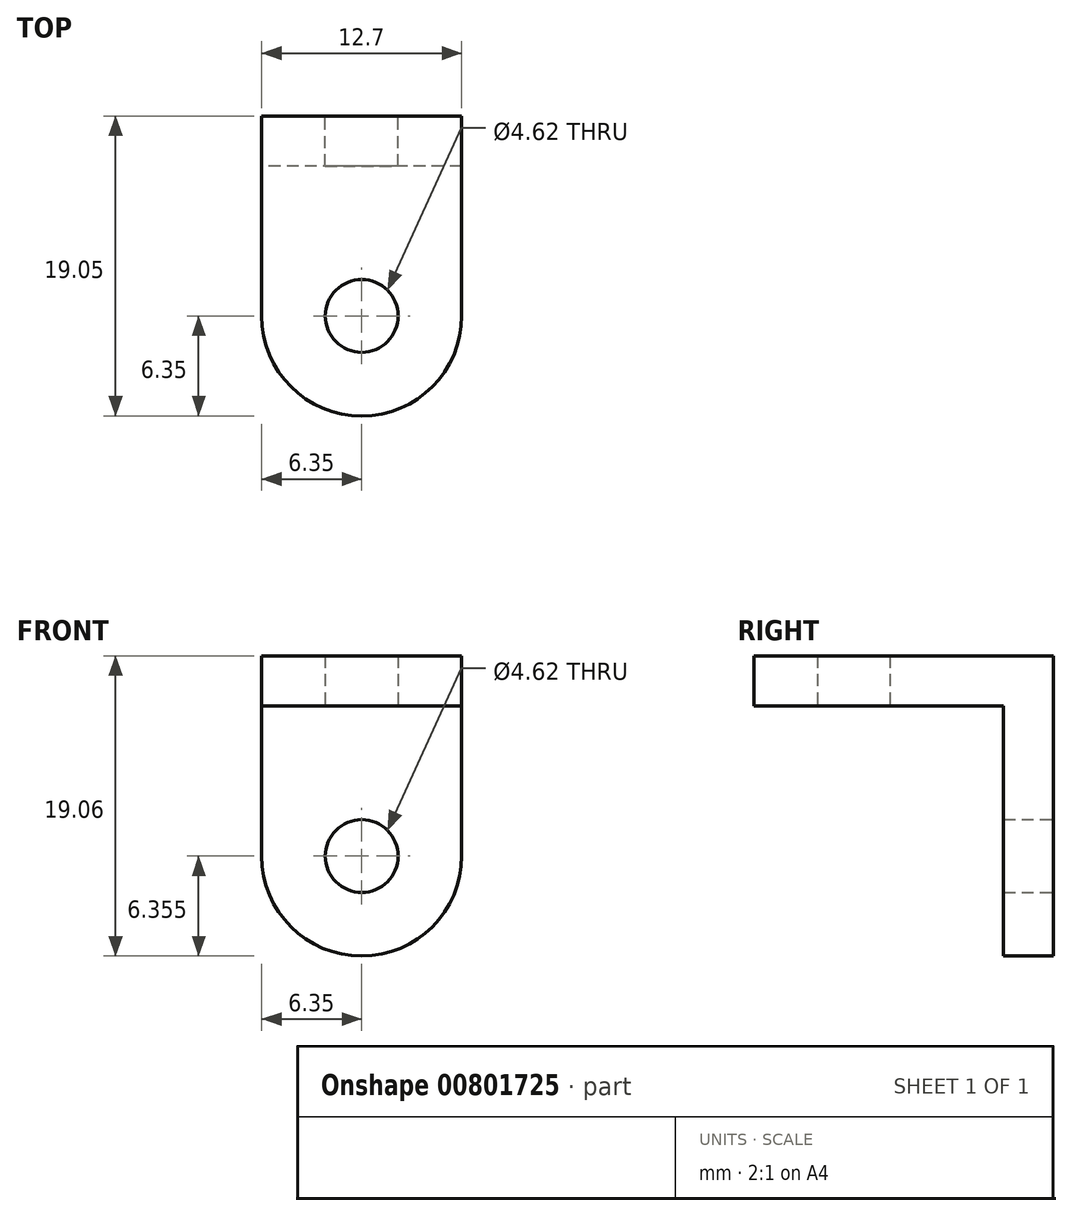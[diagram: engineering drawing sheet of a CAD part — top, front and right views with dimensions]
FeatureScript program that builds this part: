
annotation { "Feature Type Name" : "Feature", "Feature Type Description" : "" }
export const myFeature = defineFeature(function(context is Context, id is Id, definition is map)
    precondition{}
    {
        {
            var Q0;
            Q0=qCreatedBy(makeId("Top.planeOp"),FACE);
            var sketch = newSketch(context, id + "F0", { "sketchPlane" : qUnion([Q0])});
            skCircle(sketch, "E0", {"center": v(0, 0) * mm, "radius": 2.31 * mm});
            skArc(sketch, "E1", {"start": v(-6.35, 0) * mm, "mid": v(0, -6.35) * mm, "end": v(6.35, 0) * mm});
            skLineSegment(sketch, "E2", {"start": v(-6.35, 0) * mm, "end": v(-6.35, 12.7) * mm});
            skLineSegment(sketch, "E3", {"start": v(-6.35, 12.7) * mm, "end": v(6.35, 12.7) * mm});
            skLineSegment(sketch, "E4", {"start": v(6.35, 12.7) * mm, "end": v(6.35, 0) * mm});
            skSolve(sketch);
        }
        {
            var Q0;
            Q0 = qSketchRegion(id + "F0", true);
            extrude(context, id + "F1", {"entities" : qUnion([Q0]), "depth" : 3.17 * mm, "offsetDistance" : 25.4 * mm});
        }
        {
            var Q0;
            Q0=makeQuery(id+"F1.opExtrude","SWEPT_FACE",FACE,{"disambiguationData":[OSD([sQuery(id+"F0.wireOp",EDGE,"E3")])]});
            var sketch = newSketch(context, id + "F2", { "sketchPlane" : qUnion([Q0])});
            skArc(sketch, "E5", {"start": v(-6.35, -9.53) * mm, "mid": v(0, -15.88) * mm, "end": v(6.35, -9.53) * mm});
            skPoint(sketch, "E5.centerSnap0", {"position": v(0, 3.18) * mm});
            skLineSegment(sketch, "E6.bottom", {"start": v(6.35, 3.18) * mm, "end": v(-6.35, 3.18) * mm});
            skLineSegment(sketch, "E6.left", {"start": v(6.35, 3.18) * mm, "end": v(6.35, -9.53) * mm});
            skLineSegment(sketch, "E6.right", {"start": v(-6.35, 3.18) * mm, "end": v(-6.35, -9.53) * mm});
            skCircle(sketch, "E7", {"center": v(0, -9.53) * mm, "radius": 2.31 * mm});
            skSolve(sketch);
        }
        {
            var Q0;
            Q0 = qSketchRegion(id + "F2", true);
            extrude(context, id + "F3", {"entities" : qUnion([Q0]), "operationType" : NewBodyOperationType.ADD, "oppositeDirection" : true, "depth" : 3.17 * mm, "offsetDistance" : 25.4 * mm});
        }
    });
